# Revit family: Grohe_MixerWithDiverter_AllureBrilliant_24279000
name_source: partatom
category: Plumbing Fixtures
units: mm (PartAtom-declared; Revit-internal decimal feet)

## family parameters
Cut with Voids When Loaded = No
Host = Face
OmniClass Number = 23.45.05.00
OmniClass Title = Sanitary Equipment
Part Type = Normal
Room Calculation Point = No
Round Connector Dimension = Use Diameter
Shared = No

## types (1)
- ALLURE BRILLIANT Single-lever mixer with 2-way diverter (24279000)
    Assembly Code = D2010
    AssetType = Fixed
    BIMObjectName = Grohe_MixerWithDiverter_AllureBrilliant_24279000
    CO2NeutralProduction = GROHE is one of the first leading manufacturer within the sanitary industry having a CO2-neutral production.
    CWFU = 4.5
    ClassificationName = Uniclass2015
    ClassificationValue = Pr_60_75_08_54
    Color = Chrome
    Cost = 0 $
    Default Elevation = 0 mm  [stored 0 ft]
    Description = ALLURE BRILLIANT Single-lever mixer with 2-way diverter
    DocumentationCertificates = https://www.bimstore.co
    DocumentationInstallationGuide = https://www.bimstore.co
    DocumentationLiterature = https://www.bimstore.co
    DocumentationMaintenance = https://www.bimstore.co
    DocumentationTechnical = https://www.bimstore.co
    DurationUnit = Years
    Ecojoy = No
    ExpectedLife = 0
    FullRecyclabilityOfPlastic = All plastic components are fully recycable
    GROHESocialCommittment = green.grohe.com/social_engagement
    GROHESustainability = green.grohe.com
    HWFU = 4.5
    IfcExportAs = IfcPipeFitting
    IfcExportType = IfcPipeFittingType
    Keynote = N13
    Manufacturer = Grohe
    ManufacturerName = Grohe
    Model = ALLURE BRILLIANT Single-lever mixer with 2-way diverter
    ModelNumber = 24279000
    ModelReference = ALLURE BRILLIANT Single-lever mixer with 2-way diverter
    NBSDescription = Mixers
    NBSObjectName = Grohe - Mixers
    NBSReference = 90-70-10/355
    NominalDepth = 0 mm  [stored 0 ft]
    NominalHeight = 0 mm  [stored 0 ft]
    NominalLength = 0 mm  [stored 0 ft]
    PrimaryMaterial = Grohe_Chrome
    ProductNumber = 24279000
    ProductPageURL = https://www.grohe.co.uk
    ProductionYear = 2023
    SustainabilityAward = green.grohe.com/awards
    SustainabilityReport = green.grohe.com/reporting
    Type Comments = ALLURE BRILLIANT Single-lever mixer with 2-way diverter
    TypeName = ALLURE BRILLIANT Single-lever mixer with 2-way diverter
    URL = https://www.grohe.co.uk
    WarrantyDurationLabor = 0
    WarrantyDurationParts = 0
    WarrantyDurationUnit = Years
    _BSBibleVersion = 17
    _BimSpecGuid = 0
    _CurrentRevision = 1
    _DistributedBy = https://www.bimstore.co
    _ObjectUserGuide = https://www.bimstore.co

note: [stored X ft] marks values corroborated as IEEE doubles in the binary element streams (Revit-internal decimal feet)

## geometry (parser evidence)
native form markers: Sweep x3
no freeform markers — native parametric forms only
